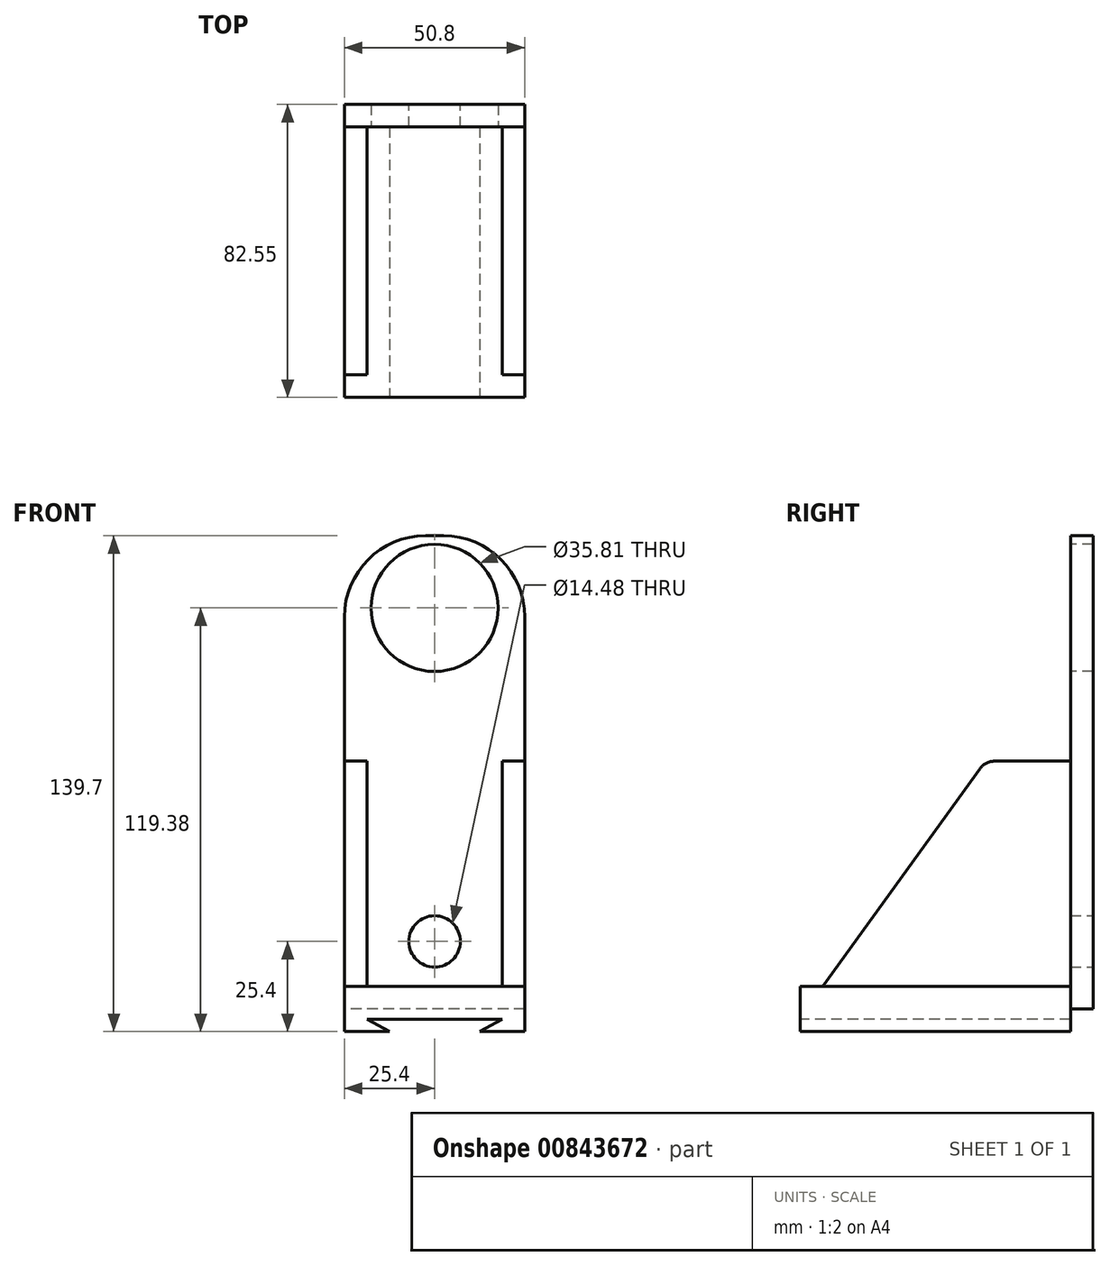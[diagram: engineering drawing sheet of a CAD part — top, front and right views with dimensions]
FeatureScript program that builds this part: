
annotation { "Feature Type Name" : "Feature", "Feature Type Description" : "" }
export const myFeature = defineFeature(function(context is Context, id is Id, definition is map)
    precondition{}
    {
        {
            var Q0;
            Q0=qCreatedBy(makeId("Top.planeOp"),FACE);
            var sketch = newSketch(context, id + "F0", { "sketchPlane" : qUnion([Q0])});
            skLineSegment(sketch, "E0.bottom", {"start": v(25.4, 38.1) * mm, "end": v(-25.4, 38.1) * mm});
            skLineSegment(sketch, "E0.top", {"start": v(25.4, -38.1) * mm, "end": v(-25.4, -38.1) * mm});
            skLineSegment(sketch, "E0.left", {"start": v(25.4, 38.1) * mm, "end": v(25.4, -38.1) * mm});
            skLineSegment(sketch, "E0.right", {"start": v(-25.4, 38.1) * mm, "end": v(-25.4, -38.1) * mm});
            skPoint(sketch, "E0.middle", {"position": v(0, 0) * mm});
            skSolve(sketch);
        }
        {
            var Q0;
            Q0=makeQuery(id+"F0.imprint","IMPRINT",FACE,{"disambiguationData":[TD([[makeQuery(id+"F0.imprint","IMPRINT",EDGE,{"derivedFrom":sQuery(id+"F0.wireOp",EDGE,"E0.bottom")}),1.0]])]});
            extrude(context, id + "F1", {"entities" : qUnion([Q0]), "depth" : 12.7 * mm, "offsetDistance" : 25.4 * mm});
        }
        {
            var Q0;
            Q0=makeQuery(id+"F1.opExtrude","SWEPT_FACE",FACE,{"disambiguationData":[OSD([sQuery(id+"F0.wireOp",EDGE,"E0.bottom")])]});
            var sketch = newSketch(context, id + "F2", { "sketchPlane" : qUnion([Q0])});
            skPoint(sketch, "E1.0", {"position": v(-25.4, 0) * mm});
            skPoint(sketch, "E2.0", {"position": v(25.4, 0) * mm});
            skLineSegment(sketch, "E3.top", {"start": v(-25.4, 139.7) * mm, "end": v(25.4, 139.7) * mm});
            skLineSegment(sketch, "E3.left", {"start": v(25.4, 6.35) * mm, "end": v(25.4, 139.7) * mm});
            skLineSegment(sketch, "E3.right", {"start": v(-25.4, 6.35) * mm, "end": v(-25.4, 139.7) * mm});
            skLineSegment(sketch, "E4", {"start": v(-25.4, 6.35) * mm, "end": v(25.4, 6.35) * mm});
            skSolve(sketch);
        }
        {
            var Q0;
            {var subQ0=sQuery(id+"F2.wireOp",EDGE,"E3.bottom");Q0=makeQuery(id+"F2.imprint","IMPRINT",FACE,{"disambiguationData":[TD([[makeQuery(id+"F2.imprint","IMPRINT",EDGE,{"derivedFrom":subQ0}),1.0]])]});}
            var Q1;
            {var subQ0=sQuery(id+"F2.wireOp",EDGE,"E3.top");Q1=makeQuery(id+"F2.imprint","IMPRINT",FACE,{"disambiguationData":[TD([[makeQuery(id+"F2.imprint","IMPRINT",EDGE,{"derivedFrom":subQ0}),-1.0]])]});}
            var Q2;
            {var subQ3=sQuery(id+"F2.wireOp",EDGE,"E4");Q2=makeQuery(id+"F2.imprint","IMPRINT",FACE,{"disambiguationData":[TD([[makeQuery(id+"F2.imprint","IMPRINT",EDGE,{"derivedFrom":subQ3}),1.0]])]});}
            extrude(context, id + "F3", {"entities" : qUnion([Q0, Q1, Q2]), "depth" : 6.35 * mm, "offsetDistance" : 25.4 * mm});
        }
        {
            var Q0;
            Q0=makeQuery(id+"F1.opExtrude","SWEPT_FACE",FACE,{"disambiguationData":[OSD([sQuery(id+"F0.wireOp",EDGE,"E0.left")])]});
            var sketch = newSketch(context, id + "F4", { "sketchPlane" : qUnion([Q0])});
            skLineSegment(sketch, "E5", {"start": v(38.1, 12.7) * mm, "end": v(-31.75, 12.7) * mm});
            skLineSegment(sketch, "E6", {"start": v(-31.75, 12.7) * mm, "end": v(14.14, 76.2) * mm});
            skPoint(sketch, "E7.0", {"position": v(38.1, 139.7) * mm});
            skLineSegment(sketch, "E8", {"start": v(38.1, 12.7) * mm, "end": v(38.1, 76.2) * mm});
            skLineSegment(sketch, "E9", {"start": v(14.14, 76.2) * mm, "end": v(38.1, 76.2) * mm});
            skSolve(sketch);
        }
        {
            var Q0;
            Q0 = qSketchRegion(id + "F4", true);
            extrude(context, id + "F5", {"entities" : qUnion([Q0]), "oppositeDirection" : true, "depth" : 6.35 * mm, "offsetDistance" : 25.4 * mm});
        }
        {
            var Q0;
            Q0=makeQuery(id+"F1.opExtrude","SWEPT_FACE",FACE,{"disambiguationData":[OSD([sQuery(id+"F0.wireOp",EDGE,"E0.right")])]});
            var sketch = newSketch(context, id + "F6", { "sketchPlane" : qUnion([Q0])});
            skLineSegment(sketch, "E10.0.0", {"start": v(-38.1, 12.7) * mm, "end": v(31.75, 12.7) * mm});
            skLineSegment(sketch, "E10.0.1", {"start": v(31.75, 12.7) * mm, "end": v(-14.14, 76.2) * mm});
            skLineSegment(sketch, "E10.0.2", {"start": v(-14.14, 76.2) * mm, "end": v(-38.1, 76.2) * mm});
            skLineSegment(sketch, "E10.0.3", {"start": v(-38.1, 76.2) * mm, "end": v(-38.1, 12.7) * mm});
            skSolve(sketch);
        }
        {
            var Q0;
            Q0=makeQuery(id+"F6.imprint","IMPRINT",FACE,{"disambiguationData":[TD([[makeQuery(id+"F6.imprint","IMPRINT",EDGE,{"derivedFrom":sQuery(id+"F6.wireOp",EDGE,"E10.0.0")}),1.0]])]});
            extrude(context, id + "F7", {"entities" : qUnion([Q0]), "oppositeDirection" : true, "depth" : 6.35 * mm, "offsetDistance" : 25.4 * mm});
        }
        {
            var Q0;
            Q0=makeQuery(id+"F7.opExtrude","SWEPT_EDGE",EDGE,{"disambiguationData":[OSD([sQuery(id+"F6.wireOp",EDGE,"E10.0.1"),sQuery(id+"F6.wireOp",EDGE,"E10.0.2")])]});
            var Q1;
            Q1=makeQuery(id+"F5.opExtrude","SWEPT_EDGE",EDGE,{"disambiguationData":[OSD([sQuery(id+"F4.wireOp",EDGE,"E6"),sQuery(id+"F4.wireOp",EDGE,"E9")])]});
            fillet(context, id + "F8", {"entities" : qUnion([Q0, Q1]), "radius" : 5.08 * mm, "tangentPropagation" : true, "allowEdgeOverflow" : false});
        }
        {
            var Q0;
            Q0=makeQuery(id+"F3.opExtrude","CAP_FACE",FACE,{"disambiguationData":[OSD([sQuery(id+"F2.wireOp",EDGE,"E3.bottom"),sQuery(id+"F2.wireOp",EDGE,"E3.top"),sQuery(id+"F2.wireOp",EDGE,"E3.left"),sQuery(id+"F2.wireOp",EDGE,"E3.right")])],"isStart":true});
            var sketch = newSketch(context, id + "F9", { "sketchPlane" : qUnion([Q0])});
            skCircle(sketch, "E11", {"center": v(0, 119.38) * mm, "radius": 17.9 * mm});
            skSolve(sketch);
        }
        {
            var Q0;
            Q0 = qSketchRegion(id + "F9", true);
            extrude(context, id + "F10", {"entities" : qUnion([Q0]), "operationType" : NewBodyOperationType.REMOVE, "oppositeDirection" : true, "depth" : 25.4 * mm, "offsetDistance" : 25.4 * mm});
        }
        {
            var Q0;
            Q0=makeQuery(id+"F1.opExtrude","SWEPT_FACE",FACE,{"disambiguationData":[OSD([sQuery(id+"F0.wireOp",EDGE,"E0.top")])]});
            var sketch = newSketch(context, id + "F11", { "sketchPlane" : qUnion([Q0])});
            skLineSegment(sketch, "E12", {"start": v(0, 0) * mm, "end": v(-12.7, 0) * mm});
            skLineSegment(sketch, "E13", {"start": v(-12.7, 0) * mm, "end": v(-19.05, 3.5) * mm});
            skLineSegment(sketch, "E14", {"start": v(-19.05, 3.5) * mm, "end": v(19.05, 3.5) * mm});
            skLineSegment(sketch, "E15", {"start": v(19.05, 3.5) * mm, "end": v(12.7, 0) * mm});
            skLineSegment(sketch, "E16", {"start": v(12.7, 0) * mm, "end": v(0, 0) * mm});
            skSolve(sketch);
        }
        {
            var Q0;
            Q0=makeQuery(id+"F11.imprint","IMPRINT",FACE,{"disambiguationData":[TD([[makeQuery(id+"F11.imprint","IMPRINT",EDGE,{"derivedFrom":sQuery(id+"F11.wireOp",EDGE,"E12")}),-1.0]])]});
            var Q1;
            Q1=makeQuery(id+"F3.opExtrude","CAP_FACE",FACE,{"disambiguationData":[OSD([sQuery(id+"F2.wireOp",EDGE,"E3.bottom"),sQuery(id+"F2.wireOp",EDGE,"E3.top"),sQuery(id+"F2.wireOp",EDGE,"E3.left"),sQuery(id+"F2.wireOp",EDGE,"E3.right")])],"isStart":false});
            var Q2;
            Q2=makeQuery(id+"F3.opExtrude","CAP_VERTEX",VERTEX,{"disambiguationData":[OSD([sQuery(id+"F2.wireOp",EDGE,"E3.bottom"),sQuery(id+"F2.wireOp",EDGE,"E3.right")])],"isStart":false});
            extrude(context, id + "F12", {"entities" : qUnion([Q0]), "operationType" : NewBodyOperationType.REMOVE, "endBound" : BoundingType.UP_TO_SURFACE, "oppositeDirection" : true, "depth" : 25.4 * mm, "endBoundEntityFace" : qUnion([Q1]), "endBoundEntityVertex" : qUnion([Q2]), "offsetDistance" : 25.4 * mm});
        }
        {
            var Q0;
            Q0=makeQuery(id+"F3.opExtrude","SWEPT_EDGE",EDGE,{"disambiguationData":[OSD([sQuery(id+"F2.wireOp",EDGE,"E3.top"),sQuery(id+"F2.wireOp",EDGE,"E3.right")])]});
            var Q1;
            Q1=makeQuery(id+"F3.opExtrude","SWEPT_EDGE",EDGE,{"disambiguationData":[OSD([sQuery(id+"F2.wireOp",EDGE,"E3.top"),sQuery(id+"F2.wireOp",EDGE,"E3.left")])]});
            fillet(context, id + "F13", {"entities" : qUnion([Q0, Q1]), "radius" : 22.86 * mm, "tangentPropagation" : true, "allowEdgeOverflow" : false});
        }
        {
            var Q0;
            Q0=makeQuery(id+"F3.opExtrude","CAP_FACE",FACE,{"disambiguationData":[OSD([sQuery(id+"F2.wireOp",EDGE,"E3.top"),sQuery(id+"F2.wireOp",EDGE,"E3.left"),sQuery(id+"F2.wireOp",EDGE,"E3.right"),sQuery(id+"F2.wireOp",EDGE,"E4")])],"isStart":false});
            var sketch = newSketch(context, id + "F14", { "sketchPlane" : qUnion([Q0])});
            skCircle(sketch, "E17", {"center": v(0, 25.4) * mm, "radius": 7.24 * mm});
            skPoint(sketch, "E17.centerSnap0", {"position": v(0, 6.35) * mm});
            skSolve(sketch);
        }
        {
            var Q0;
            Q0=makeQuery(id+"F14.imprint","IMPRINT",FACE,{"disambiguationData":[TD([[makeQuery(id+"F14.imprint","IMPRINT",EDGE,{"derivedFrom":sQuery(id+"F14.wireOp",EDGE,"E17")}),1.0]])]});
            var Q1;
            Q1=sQuery(id+"F14.wireOp",EDGE,"E17");
            extrude(context, id + "F15", {"entities" : qUnion([Q0]), "operationType" : NewBodyOperationType.REMOVE, "surfaceEntities" : qUnion([Q1]), "endBound" : BoundingType.THROUGH_ALL, "oppositeDirection" : true, "depth" : 25.4 * mm, "offsetDistance" : 25.4 * mm});
        }
    });
